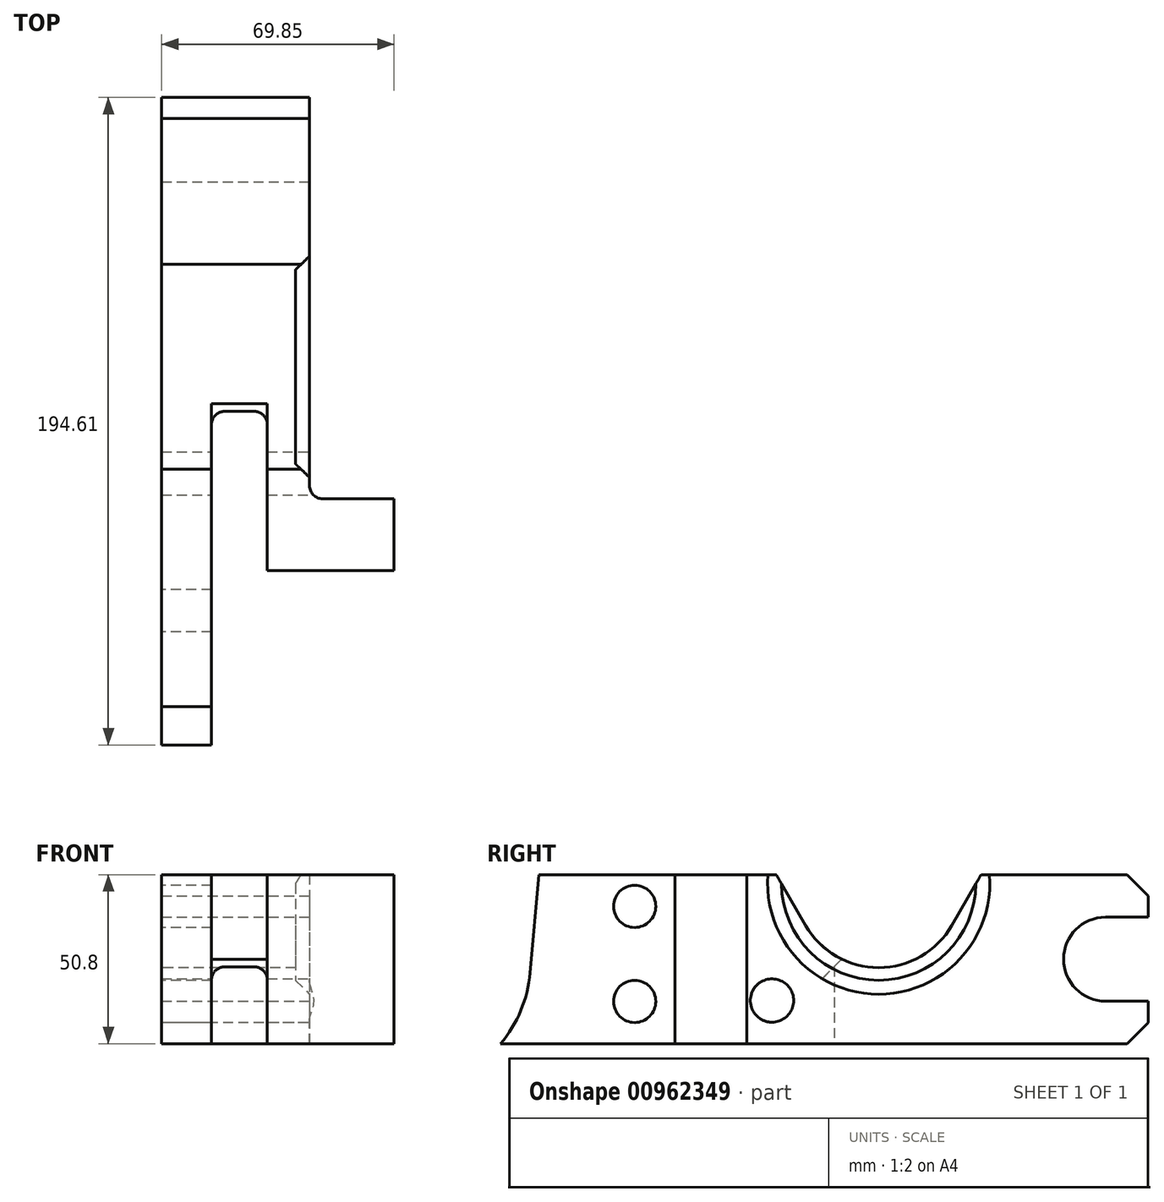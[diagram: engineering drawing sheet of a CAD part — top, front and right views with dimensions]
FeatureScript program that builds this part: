
annotation { "Feature Type Name" : "Feature", "Feature Type Description" : "" }
export const myFeature = defineFeature(function(context is Context, id is Id, definition is map)
    precondition{}
    {
        {
            var Q0;
            Q0=qCreatedBy(makeId("Top.planeOp"),FACE);
            var sketch = newSketch(context, id + "F0", { "sketchPlane" : qUnion([Q0])});
            skLineSegment(sketch, "E0.top", {"start": v(0, 120.65) * mm, "end": v(44.45, 120.65) * mm});
            skLineSegment(sketch, "E0.left", {"start": v(0, 0) * mm, "end": v(0, 120.65) * mm});
            skLineSegment(sketch, "E0.right", {"start": v(44.45, 0) * mm, "end": v(44.45, 120.65) * mm});
            skLineSegment(sketch, "E1.bottom", {"start": v(44.45, 0) * mm, "end": v(69.85, 0) * mm});
            skLineSegment(sketch, "E1.top", {"start": v(31.75, -21.6) * mm, "end": v(69.85, -21.6) * mm});
            skLineSegment(sketch, "E1.left", {"start": v(0, 0) * mm, "end": v(0, -21.6) * mm});
            skLineSegment(sketch, "E1.right", {"start": v(69.85, 0) * mm, "end": v(69.85, -21.6) * mm});
            skLineSegment(sketch, "E2.top", {"start": v(0, -73.96) * mm, "end": v(14.99, -73.96) * mm});
            skLineSegment(sketch, "E2.left", {"start": v(0, -21.6) * mm, "end": v(0, -73.96) * mm});
            skLineSegment(sketch, "E3", {"start": v(14.99, 26.28) * mm, "end": v(31.75, 26.28) * mm});
            skLineSegment(sketch, "E4", {"start": v(31.75, 26.28) * mm, "end": v(31.75, -21.6) * mm});
            skLineSegment(sketch, "E5", {"start": v(14.99, 26.28) * mm, "end": v(14.99, -73.96) * mm});
            skSolve(sketch);
        }
        {
            var Q0;
            Q0=makeQuery(id+"F0.imprint","IMPRINT",FACE,{"disambiguationData":[TD([[makeQuery(id+"F0.imprint","IMPRINT",EDGE,{"derivedFrom":sQuery(id+"F0.wireOp",EDGE,"E0.top")}),-1.0]])]});
            extrude(context, id + "F1", {"entities" : qUnion([Q0]), "depth" : 50.8 * mm, "offsetDistance" : 25.4 * mm});
        }
        {
            var Q0;
            Q0=makeQuery(id+"F1.opExtrude","SWEPT_EDGE",EDGE,{"disambiguationData":[OSD([sQuery(id+"F0.wireOp",EDGE,"E0.right"),sQuery(id+"F0.wireOp",EDGE,"E1.bottom")])]});
            var Q1;
            Q1=makeQuery(id+"F1.opExtrude","SWEPT_EDGE",EDGE,{"disambiguationData":[OSD([sQuery(id+"F0.wireOp",EDGE,"E3"),sQuery(id+"F0.wireOp",EDGE,"E5")])]});
            var Q2;
            Q2=makeQuery(id+"F1.opExtrude","SWEPT_EDGE",EDGE,{"disambiguationData":[OSD([sQuery(id+"F0.wireOp",EDGE,"E3"),sQuery(id+"F0.wireOp",EDGE,"E4")])]});
            fillet(context, id + "F2", {"entities" : qUnion([Q0, Q1, Q2]), "radius" : 3.96 * mm, "tangentPropagation" : true, "allowEdgeOverflow" : false});
        }
        {
            var Q0;
            Q0=makeQuery(id+"F1.opExtrude","CAP_EDGE",EDGE,{"disambiguationData":[OSD([sQuery(id+"F0.wireOp",EDGE,"E0.top")])],"isStart":false});
            var Q1;
            Q1=makeQuery(id+"F1.opExtrude","CAP_EDGE",EDGE,{"disambiguationData":[OSD([sQuery(id+"F0.wireOp",EDGE,"E0.top")])],"isStart":true});
            chamfer(context, id + "F3", {"entities" : qUnion([Q0, Q1]), "width" : 6.35 * mm, "tangentPropagation" : true});
        }
        {
            var Q0;
            Q0=makeQuery(id+"F1.opExtrude","SWEPT_FACE",FACE,{"disambiguationData":[OSD([sQuery(id+"F0.wireOp",EDGE,"E0.right")])]});
            var sketch = newSketch(context, id + "F4", { "sketchPlane" : qUnion([Q0])});
            skLineSegment(sketch, "E6.bottom", {"start": v(107.89, 38.04) * mm, "end": v(120.65, 38.04) * mm});
            skLineSegment(sketch, "E6.top", {"start": v(107.89, 12.76) * mm, "end": v(120.65, 12.76) * mm});
            skLineSegment(sketch, "E6.right", {"start": v(120.65, 38.04) * mm, "end": v(120.65, 12.76) * mm});
            skArc(sketch, "E7", {"start": v(107.89, 38.04) * mm, "mid": v(95.25, 25.4) * mm, "end": v(107.89, 12.76) * mm});
            skLineSegment(sketch, "E8", {"start": v(-73.96, 25.4) * mm, "end": v(120.65, 25.4) * mm, "construction": true});
            skPoint(sketch, "E9", {"position": v(95.25, 25.4) * mm});
            skSolve(sketch);
        }
        {
            var Q0;
            Q0 = qSketchRegion(id + "F4", true);
            extrude(context, id + "F5", {"entities" : qUnion([Q0]), "operationType" : NewBodyOperationType.REMOVE, "endBound" : BoundingType.THROUGH_ALL, "oppositeDirection" : true, "depth" : 25.4 * mm, "offsetDistance" : 25.4 * mm});
        }
        {
            var Q0;
            Q0=makeQuery(id+"F1.opExtrude","SWEPT_FACE",FACE,{"disambiguationData":[OSD([sQuery(id+"F0.wireOp",EDGE,"E1.right")])]});
            var sketch = newSketch(context, id + "F6", { "sketchPlane" : qUnion([Q0])});
            skPoint(sketch, "E10", {"position": v(7.62, 12.95) * mm});
            skSolve(sketch);
        }
        {
            var Q0;
            Q0=sQuery(id+"F6.wireOp",VERTEX,"E10");
            var Q1;
            Q1=makeQuery(id+"F1.opExtrude","SWEPT_BODY",BODY,{"disambiguationData":[OSD([sQuery(id+"F0.wireOp",EDGE,"E0.top"),sQuery(id+"F0.wireOp",EDGE,"E0.left"),sQuery(id+"F0.wireOp",EDGE,"E0.right"),sQuery(id+"F0.wireOp",EDGE,"E1.bottom"),sQuery(id+"F0.wireOp",EDGE,"E1.top"),sQuery(id+"F0.wireOp",EDGE,"E1.left"),sQuery(id+"F0.wireOp",EDGE,"E1.right"),sQuery(id+"F0.wireOp",EDGE,"E2.top"),sQuery(id+"F0.wireOp",EDGE,"E2.left"),sQuery(id+"F0.wireOp",EDGE,"E3"),sQuery(id+"F0.wireOp",EDGE,"E4"),sQuery(id+"F0.wireOp",EDGE,"E5")])]});
            hole(context, id + "F7", {"style" : HoleStyle.SIMPLE, "endStyle" : HoleEndStyle.THROUGH, "holeDiameter" : 13.03 * mm, "majorDiameter" : 6.35 * mm, "isTappedThrough" : true, "tappedDepth" : 12.7 * mm, "tapClearance" : 3, "startFromSketch" : true, "locations" : qUnion([Q0]), "scope" : qUnion([Q1])});
        }
        {
            var Q0;
            Q0=makeQuery(id+"F1.opExtrude","SWEPT_FACE",FACE,{"disambiguationData":[OSD([sQuery(id+"F0.wireOp",EDGE,"E0.left"),sQuery(id+"F0.wireOp",EDGE,"E1.left"),sQuery(id+"F0.wireOp",EDGE,"E2.left")])]});
            var sketch = newSketch(context, id + "F8", { "sketchPlane" : qUnion([Q0])});
            skLineSegment(sketch, "E11", {"start": v(-70.48, 50.8) * mm, "end": v(-61.68, 35.56) * mm});
            skLineSegment(sketch, "E12", {"start": v(-8.9, 50.8) * mm, "end": v(-17.7, 35.56) * mm});
            skArc(sketch, "E13", {"start": v(-61.68, 35.56) * mm, "mid": v(-39.69, 22.86) * mm, "end": v(-17.7, 35.56) * mm});
            skPoint(sketch, "E13.first.point", {"position": v(-61.68, 35.56) * mm});
            skPoint(sketch, "E13.second.point", {"position": v(-17.7, 35.56) * mm});
            skPoint(sketch, "E14.orphan", {"position": v(-52.89, 20.32) * mm});
            skPoint(sketch, "E15.orphan", {"position": v(-26.49, 20.32) * mm});
            skLineSegment(sketch, "E16", {"start": v(-39.69, 48.26) * mm, "end": v(-39.69, 0) * mm, "construction": true});
            skPoint(sketch, "E16.endSnap0", {"position": v(-39.69, 22.86) * mm});
            skLineSegment(sketch, "E17", {"start": v(-70.48, 50.8) * mm, "end": v(-8.9, 50.8) * mm});
            skSolve(sketch);
        }
        {
            var Q0;
            Q0 = qSketchRegion(id + "F8", true);
            extrude(context, id + "F9", {"entities" : qUnion([Q0]), "operationType" : NewBodyOperationType.REMOVE, "endBound" : BoundingType.THROUGH_ALL, "oppositeDirection" : true, "depth" : 25.4 * mm, "offsetDistance" : 25.4 * mm});
        }
        {
            var Q0;
            Q0=makeQuery(id+"F1.opExtrude","SWEPT_FACE",FACE,{"disambiguationData":[OSD([sQuery(id+"F0.wireOp",EDGE,"E1.right")])]});
            var sketch = newSketch(context, id + "F10", { "sketchPlane" : qUnion([Q0])});
            skCircle(sketch, "E18", {"center": v(39.69, 48.26) * mm, "radius": 29.21 * mm});
            skSolve(sketch);
        }
        {
            var Q0;
            Q0 = qSketchRegion(id + "F10", true);
            extrude(context, id + "F11", {"entities" : qUnion([Q0]), "operationType" : NewBodyOperationType.REMOVE, "oppositeDirection" : true, "depth" : 29.6 * mm, "offsetDistance" : 25.4 * mm});
        }
        {
            var Q0;
            Q0=makeQuery(id+"F11.boolean.opBoolean","INTERSECT",EDGE,{"derivedFrom":[makeQuery(id+"F1.opExtrude","SWEPT_FACE",FACE,{"disambiguationData":[OSD([sQuery(id+"F0.wireOp",EDGE,"E0.right")])]}),makeQuery(id+"F11.opExtrude","SWEPT_FACE",FACE,{"disambiguationData":[OSD([sQuery(id+"F10.wireOp",EDGE,"E18")])]})]});
            chamfer(context, id + "F12", {"entities" : qUnion([Q0]), "width" : 4.2 * mm, "tangentPropagation" : true});
        }
        {
            var Q0;
            Q0=makeQuery(id+"F1.opExtrude","SWEPT_FACE",FACE,{"disambiguationData":[OSD([sQuery(id+"F0.wireOp",EDGE,"E5")])]});
            var sketch = newSketch(context, id + "F13", { "sketchPlane" : qUnion([Q0])});
            skArc(sketch, "E19", {"start": v(-73.96, 0) * mm, "mid": v(-67.87, 9.97) * mm, "end": v(-65.07, 21.31) * mm});
            skLineSegment(sketch, "E20", {"start": v(-65.07, 21.31) * mm, "end": v(-62.5, 50.8) * mm});
            skLineSegment(sketch, "E21", {"start": v(-62.5, 50.8) * mm, "end": v(-73.96, 50.8) * mm});
            skLineSegment(sketch, "E22", {"start": v(-73.96, 50.8) * mm, "end": v(-73.96, 0) * mm});
            skSolve(sketch);
        }
        {
            var Q0;
            Q0 = qSketchRegion(id + "F13", true);
            extrude(context, id + "F14", {"entities" : qUnion([Q0]), "operationType" : NewBodyOperationType.REMOVE, "endBound" : BoundingType.THROUGH_ALL, "oppositeDirection" : true, "depth" : 25.4 * mm, "offsetDistance" : 25.4 * mm});
        }
        {
            var Q0;
            Q0=makeQuery(id+"F1.opExtrude","SWEPT_FACE",FACE,{"disambiguationData":[OSD([sQuery(id+"F0.wireOp",EDGE,"E5")])]});
            var sketch = newSketch(context, id + "F15", { "sketchPlane" : qUnion([Q0])});
            skPoint(sketch, "E23", {"position": v(26.28, 26.69) * mm});
            skLineSegment(sketch, "E24", {"start": v(26.28, 26.69) * mm, "end": v(19.26, 19.67) * mm, "construction": true});
            skLineSegment(sketch, "E25", {"start": v(22.86, 19.67) * mm, "end": v(11.93, 19.67) * mm});
            skLineSegment(sketch, "E26", {"start": v(11.93, 19.67) * mm, "end": v(11.93, 38.74) * mm});
            skLineSegment(sketch, "E27", {"start": v(11.93, 38.74) * mm, "end": v(41.92, 38.74) * mm});
            skLineSegment(sketch, "E28", {"start": v(26.28, 26.69) * mm, "end": v(38.33, 38.74) * mm, "construction": true});
            skLineSegment(sketch, "E29.0", {"start": v(22.86, 19.67) * mm, "end": v(41.92, 38.74) * mm});
            skSolve(sketch);
        }
        {
            var Q0;
            Q0 = qSketchRegion(id + "F15", true);
            var Q1;
            Q1=makeQuery(id+"F1.opExtrude","SWEPT_FACE",FACE,{"disambiguationData":[OSD([sQuery(id+"F0.wireOp",EDGE,"E4")])]});
            extrude(context, id + "F16", {"entities" : qUnion([Q0]), "operationType" : NewBodyOperationType.REMOVE, "endBound" : BoundingType.UP_TO_SURFACE, "depth" : 25.4 * mm, "endBoundEntityFace" : qUnion([Q1]), "offsetDistance" : 25.4 * mm});
        }
        {
            var Q0;
            Q0=makeQuery(id+"F1.opExtrude","SWEPT_FACE",FACE,{"disambiguationData":[OSD([sQuery(id+"F0.wireOp",EDGE,"E0.left"),sQuery(id+"F0.wireOp",EDGE,"E1.left"),sQuery(id+"F0.wireOp",EDGE,"E2.left")])]});
            var sketch = newSketch(context, id + "F17", { "sketchPlane" : qUnion([Q0])});
            skCircle(sketch, "E30", {"center": v(33.65, 12.7) * mm, "radius": 6.35 * mm});
            skPoint(sketch, "E31", {"position": v(-7.62, 12.95) * mm});
            skCircle(sketch, "E32", {"center": v(33.65, 41.28) * mm, "radius": 6.35 * mm});
            skSolve(sketch);
        }
        {
            var Q0;
            Q0 = qSketchRegion(id + "F17", true);
            extrude(context, id + "F18", {"entities" : qUnion([Q0]), "operationType" : NewBodyOperationType.REMOVE, "endBound" : BoundingType.THROUGH_ALL, "oppositeDirection" : true, "depth" : 25.4 * mm, "offsetDistance" : 25.4 * mm});
        }
    });
